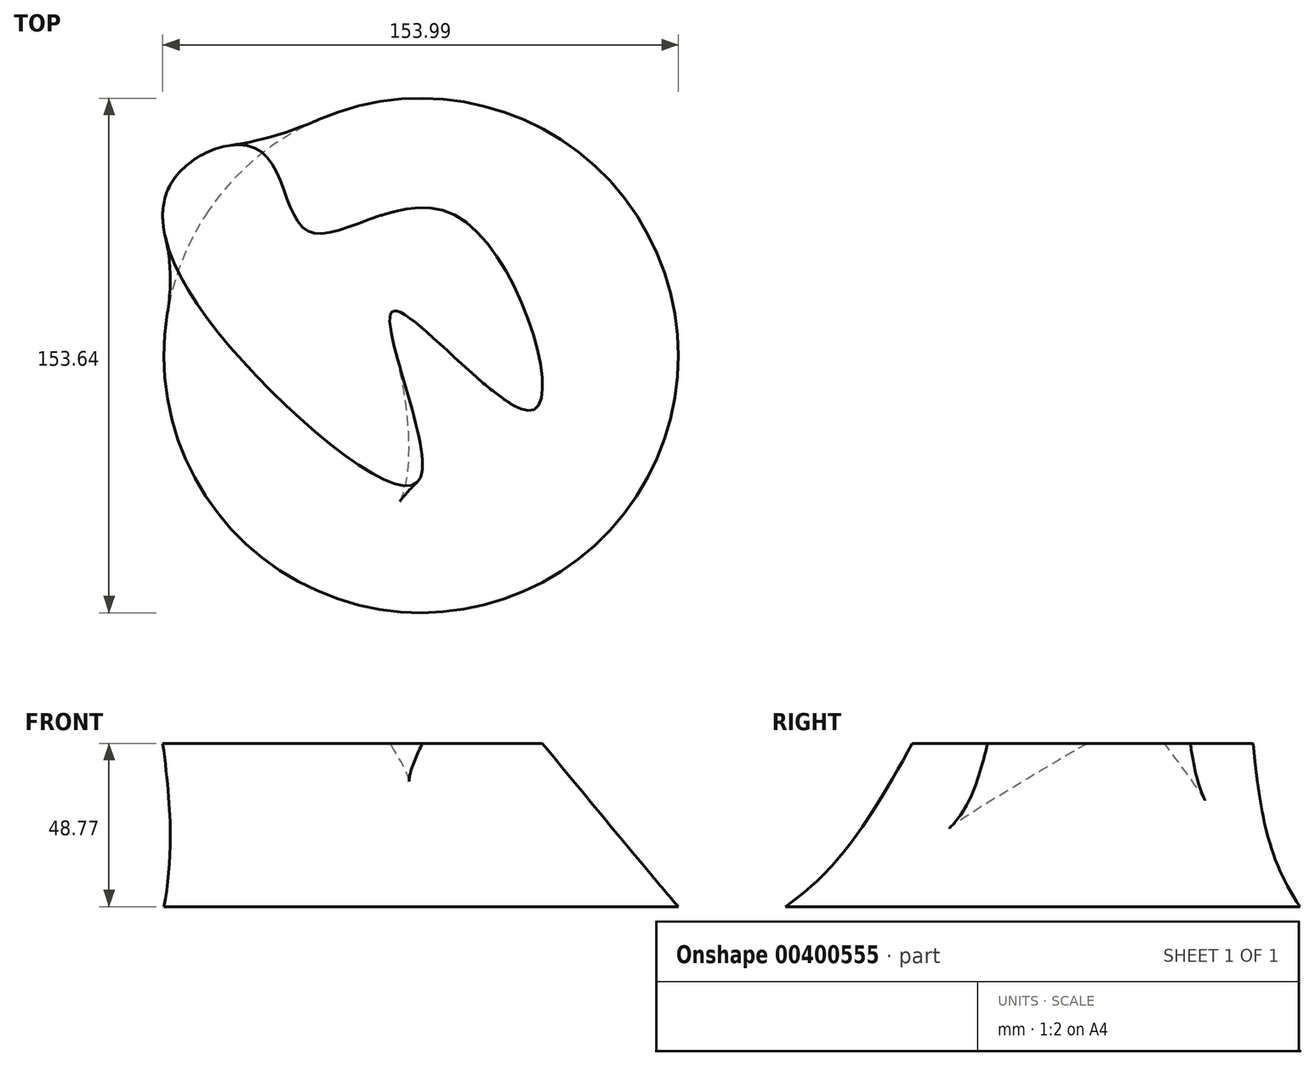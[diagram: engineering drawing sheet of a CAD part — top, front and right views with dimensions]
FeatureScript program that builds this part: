
annotation { "Feature Type Name" : "Feature", "Feature Type Description" : "" }
export const myFeature = defineFeature(function(context is Context, id is Id, definition is map)
    precondition{}
    {
        {
            var Q0;
            Q0=qCreatedBy(makeId("Top.planeOp"),FACE);
            cPlane(context, id + "F0", {"entities" : qUnion([Q0]), "cplaneType" : CPlaneType.OFFSET, "offset" : 48.77 * mm, "width" : 152.4 * mm, "height" : 152.4 * mm});
        }
        {
            var Q0;
            Q0=qCreatedBy(makeId("Top.planeOp"),FACE);
            var sketch = newSketch(context, id + "F1", { "sketchPlane" : qUnion([Q0])});
            skCircle(sketch, "E0", {"center": v(0, 0) * mm, "radius": 76.82 * mm});
            skSolve(sketch);
        }
        {
            var Q0;
            Q0=qCreatedBy(id+"F0.planeOp",FACE);
            var sketch = newSketch(context, id + "F2", { "sketchPlane" : qUnion([Q0])});
            skFitSpline(sketch, "E1", {"points": [v(-74.9, 50.98) * mm, v(-50.5, -4.73) * mm, v(0, -35.92) * mm, v(-8.36, 13.26) * mm, v(33.08, -16.4) * mm, v(10.45, 41.74) * mm, v(-33.3, 36.92) * mm, v(-47.87, 60.94) * mm, v(-74.9, 50.98) * mm]});
            skSolve(sketch);
        }
        {
            var Q0;
            Q0=makeQuery(id+"F2.imprint","IMPRINT",FACE,{"disambiguationData":[TD([[makeQuery(id+"F2.imprint","IMPRINT",EDGE,{"derivedFrom":sQuery(id+"F2.wireOp",EDGE,"E1")}),1.0]])]});
            var Q1;
            Q1=makeQuery(id+"F1.imprint","IMPRINT",FACE,{"disambiguationData":[TD([[makeQuery(id+"F1.imprint","IMPRINT",EDGE,{"derivedFrom":sQuery(id+"F1.wireOp",EDGE,"E0")}),1.0]])]});
            loft(context, id + "F3", {"sheetProfilesArray" : [{ "sheetProfileEntities" : qUnion([Q0]) }, { "sheetProfileEntities" : qUnion([Q1]) }]});
        }
    });
